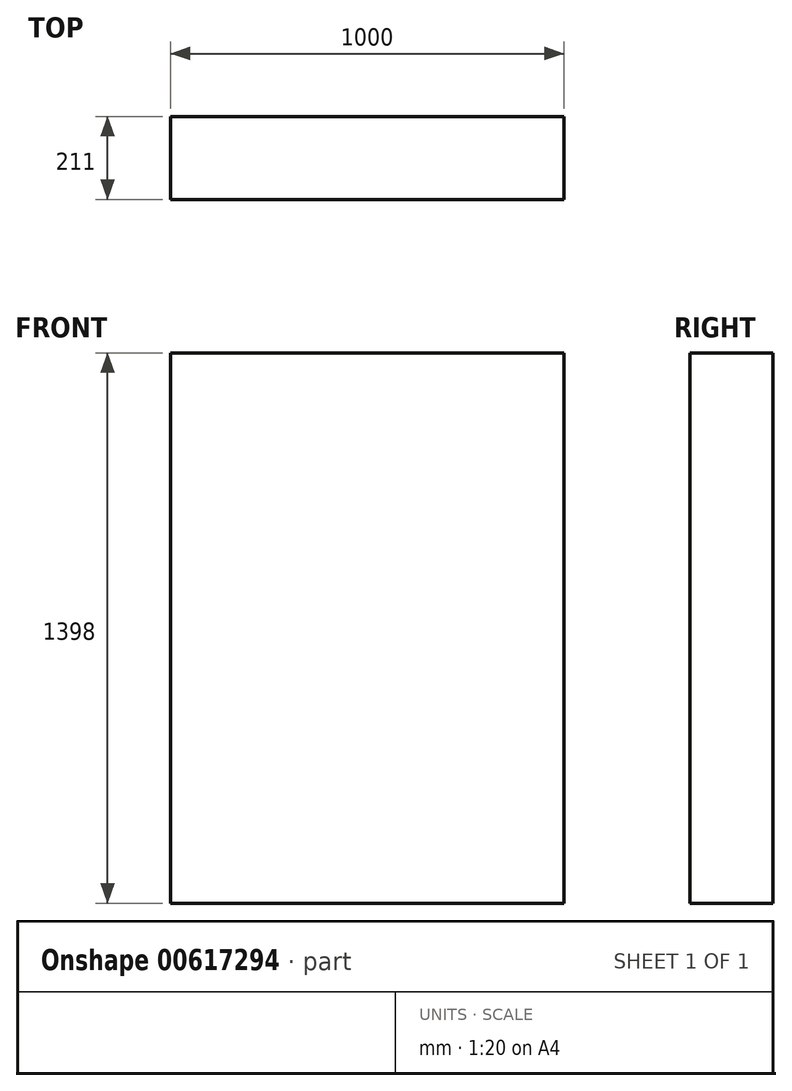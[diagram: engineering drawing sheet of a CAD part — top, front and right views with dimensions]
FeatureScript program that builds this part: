
annotation { "Feature Type Name" : "Feature", "Feature Type Description" : "" }
export const myFeature = defineFeature(function(context is Context, id is Id, definition is map)
    precondition{}
    {
        {
            var Q0;
            Q0=qCreatedBy(makeId("Top.planeOp"),FACE);
            var sketch = newSketch(context, id + "F0", { "sketchPlane" : qUnion([Q0])});
            skLineSegment(sketch, "E0.bottom", {"start": v(-496.02, 49.5) * mm, "end": v(503.98, 49.5) * mm});
            skLineSegment(sketch, "E0.top", {"start": v(-496.02, -161.5) * mm, "end": v(503.98, -161.5) * mm});
            skLineSegment(sketch, "E0.left", {"start": v(-496.02, 49.5) * mm, "end": v(-496.02, -161.5) * mm});
            skLineSegment(sketch, "E0.right", {"start": v(503.98, 49.5) * mm, "end": v(503.98, -161.5) * mm});
            skSolve(sketch);
        }
        {
            var Q0;
            Q0 = qSketchRegion(id + "F0", true);
            extrude(context, id + "F1", {"entities" : qUnion([Q0]), "depth" : 1398 * mm, "offsetDistance" : 25 * mm});
        }
    });
